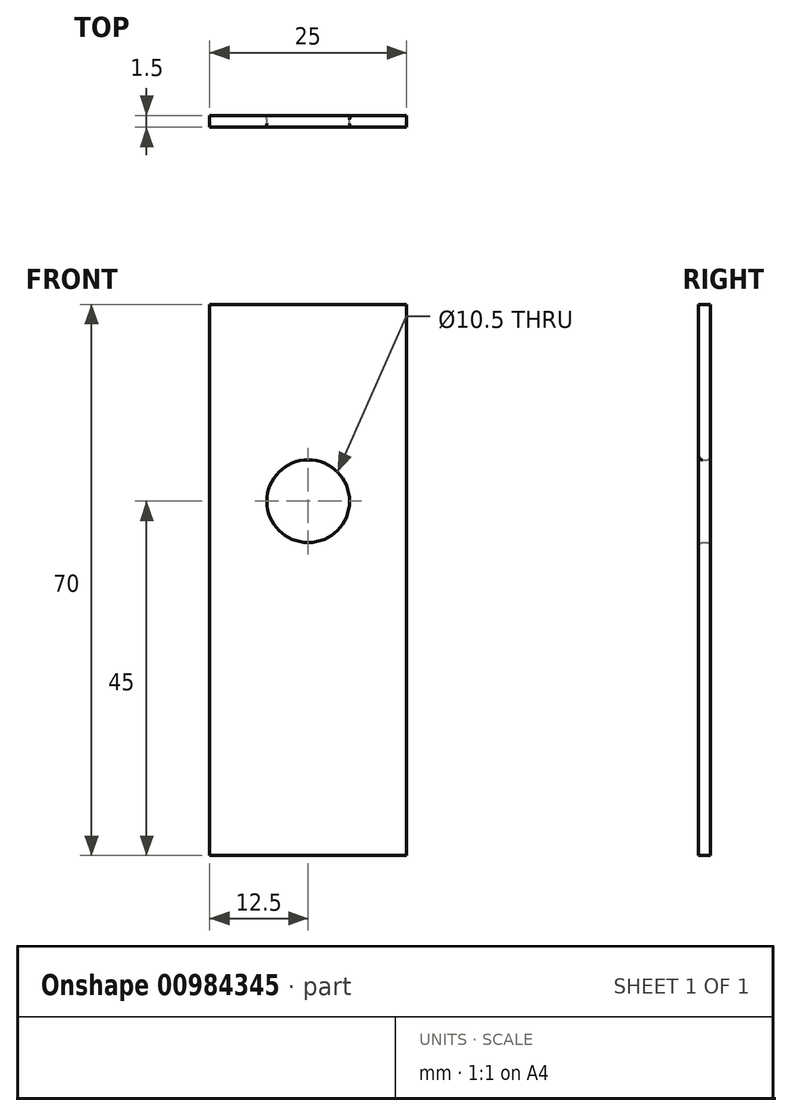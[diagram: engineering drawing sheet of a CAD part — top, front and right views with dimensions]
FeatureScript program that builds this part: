
annotation { "Feature Type Name" : "Feature", "Feature Type Description" : "" }
export const myFeature = defineFeature(function(context is Context, id is Id, definition is map)
    precondition{}
    {
        {
            var Q0;
            Q0=qCreatedBy(makeId("Front.planeOp"),FACE);
            var sketch = newSketch(context, id + "F0", { "sketchPlane" : qUnion([Q0])});
            skLineSegment(sketch, "E0.bottom", {"start": v(-12.5, 35) * mm, "end": v(12.5, 35) * mm});
            skLineSegment(sketch, "E0.top", {"start": v(-12.5, -35) * mm, "end": v(12.5, -35) * mm});
            skLineSegment(sketch, "E0.left", {"start": v(-12.5, 35) * mm, "end": v(-12.5, -35) * mm});
            skLineSegment(sketch, "E0.right", {"start": v(12.5, 35) * mm, "end": v(12.5, -35) * mm});
            skPoint(sketch, "E0.middle", {"position": v(0, 0) * mm});
            skCircle(sketch, "E1", {"center": v(0, 10) * mm, "radius": 5.25 * mm});
            skSolve(sketch);
        }
        {
            var Q0;
            Q0=makeQuery(id+"F0.imprint","IMPRINT",FACE,{"disambiguationData":[TD([[makeQuery(id+"F0.imprint","IMPRINT",EDGE,{"derivedFrom":sQuery(id+"F0.wireOp",EDGE,"E0.bottom")}),-1.0]])]});
            extrude(context, id + "F1", {"entities" : qUnion([Q0]), "depth" : 1.5 * mm, "offsetDistance" : 25 * mm});
        }
        {
            var Q0;
            Q0=makeQuery(id+"F1.opExtrude","CAP_EDGE",EDGE,{"disambiguationData":[OSD([sQuery(id+"F0.wireOp",EDGE,"E1")])],"isStart":true});
            var Q1;
            Q1=makeQuery(id+"F1.opExtrude","CAP_EDGE",EDGE,{"disambiguationData":[OSD([sQuery(id+"F0.wireOp",EDGE,"E1")])],"isStart":false});
            fillet(context, id + "F2", {"entities" : qUnion([Q0, Q1]), "radius" : 0.5 * mm, "tangentPropagation" : true, "allowEdgeOverflow" : false});
        }
    });
